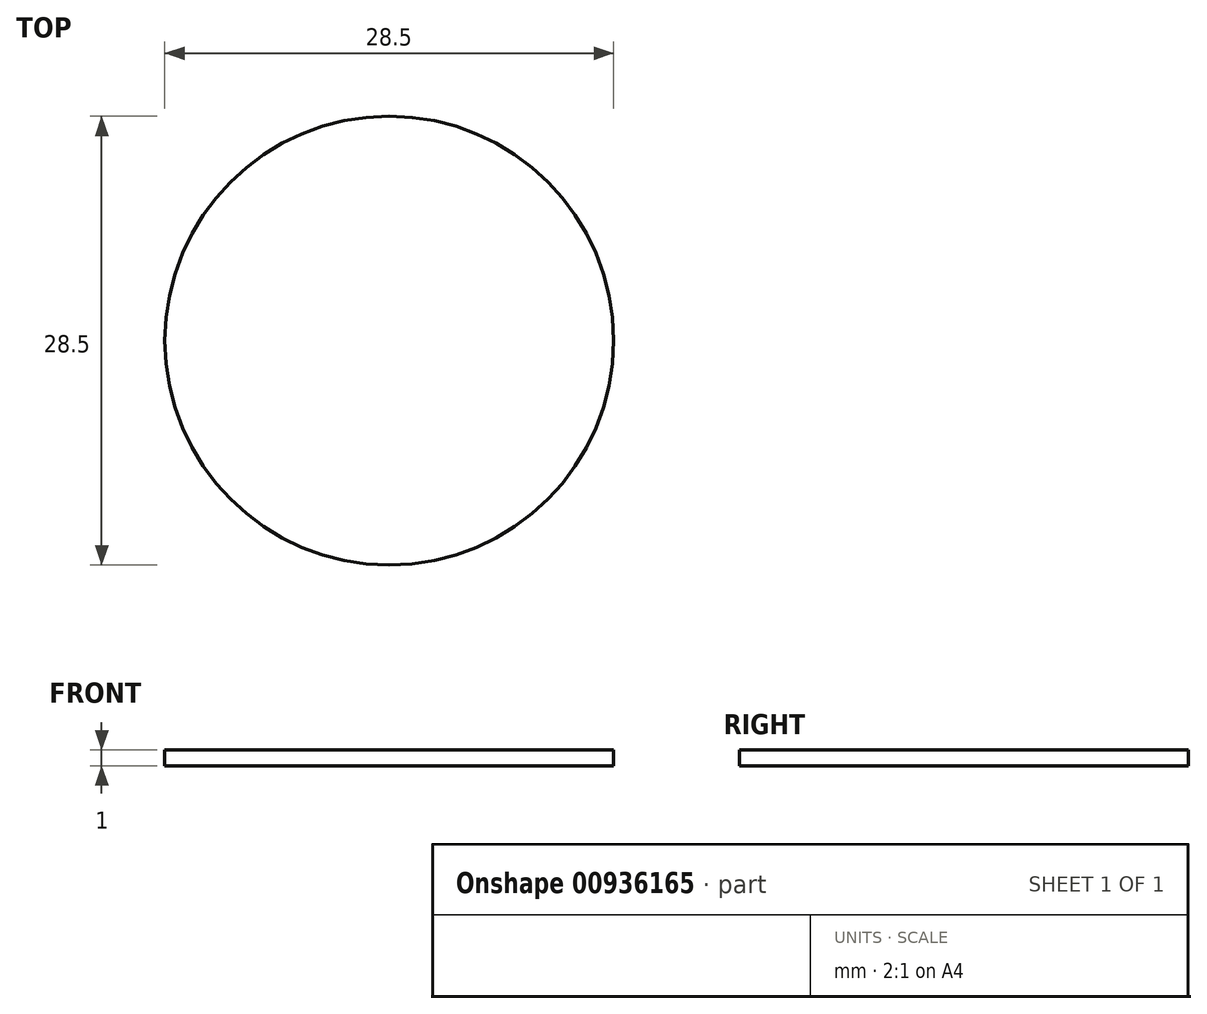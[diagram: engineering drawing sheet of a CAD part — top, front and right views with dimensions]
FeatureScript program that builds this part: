
annotation { "Feature Type Name" : "Feature", "Feature Type Description" : "" }
export const myFeature = defineFeature(function(context is Context, id is Id, definition is map)
    precondition{}
    {
        {
            var Q0;
            Q0=qCreatedBy(makeId("Top.planeOp"),FACE);
            var sketch = newSketch(context, id + "F0", { "sketchPlane" : qUnion([Q0])});
            skCircle(sketch, "E0", {"center": v(0, 0) * mm, "radius": 14.25 * mm});
            skSolve(sketch);
        }
        {
            var Q0;
            Q0 = qSketchRegion(id + "F0", true);
            extrude(context, id + "F1", {"entities" : qUnion([Q0]), "depth" : 1 * mm, "offsetDistance" : 25 * mm});
        }
    });
